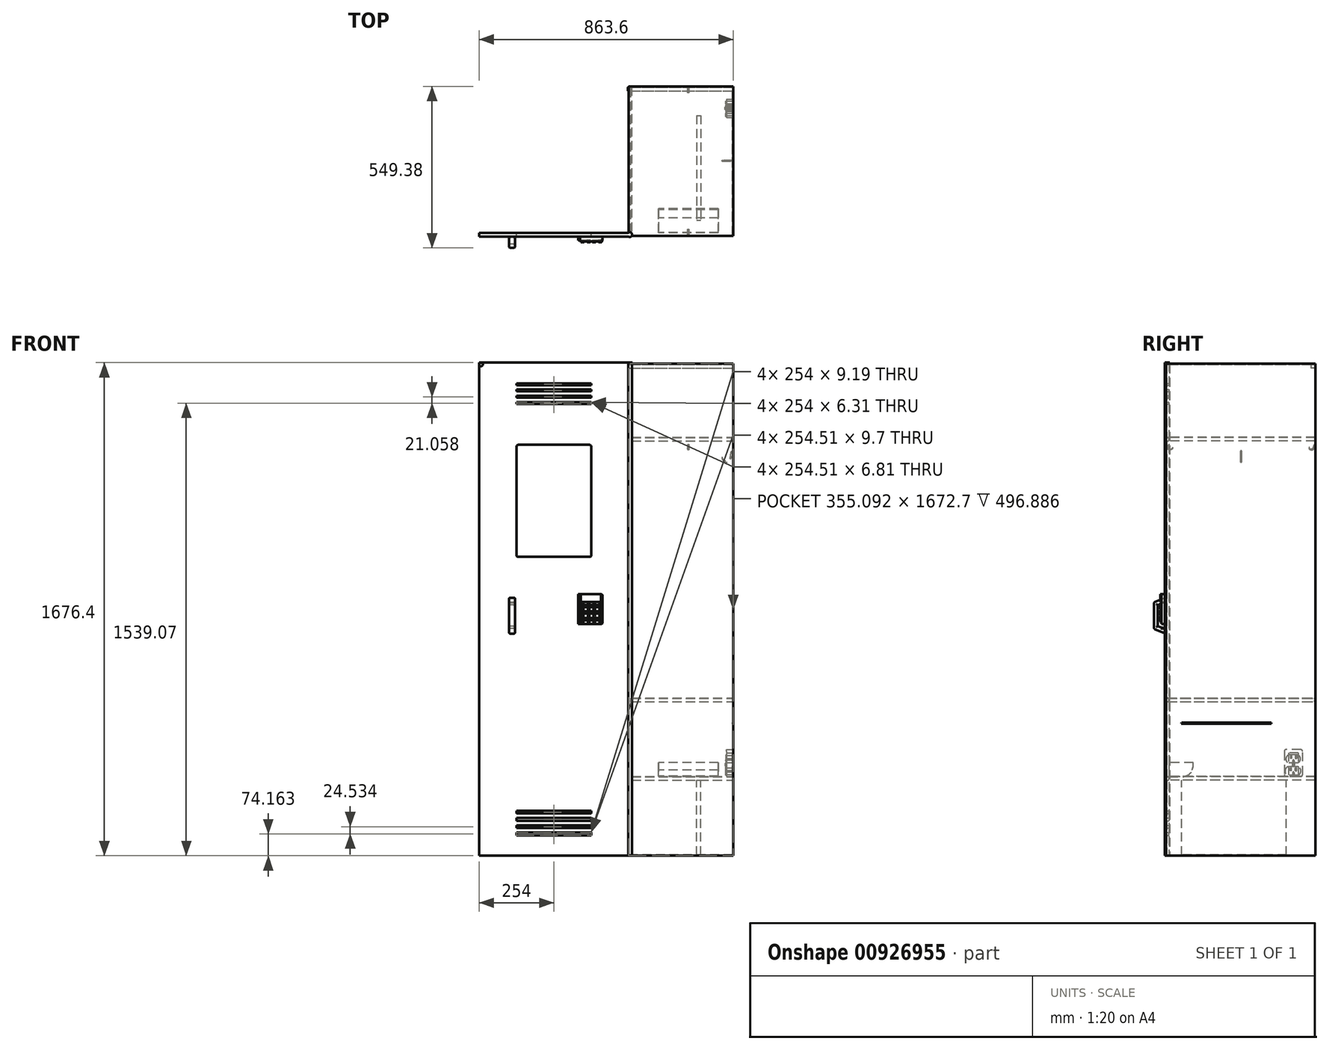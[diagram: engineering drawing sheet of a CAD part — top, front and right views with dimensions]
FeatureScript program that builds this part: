
annotation { "Feature Type Name" : "Feature", "Feature Type Description" : "" }
export const myFeature = defineFeature(function(context is Context, id is Id, definition is map)
    precondition{}
    {
        {
            var Q0;
            Q0=qCreatedBy(makeId("Front.planeOp"),FACE);
            var sketch = newSketch(context, id + "F0", { "sketchPlane" : qUnion([Q0])});
            skLineSegment(sketch, "E0.bottom", {"start": v(0, 0) * mm, "end": v(-508, 0) * mm});
            skLineSegment(sketch, "E0.top", {"start": v(0, 1676.4) * mm, "end": v(-508, 1676.4) * mm});
            skLineSegment(sketch, "E0.left", {"start": v(0, 0) * mm, "end": v(0, 1676.4) * mm});
            skLineSegment(sketch, "E0.right", {"start": v(-508, 0) * mm, "end": v(-508, 1676.4) * mm});
            skLineSegment(sketch, "E1", {"start": v(0, 1676.4) * mm, "end": v(0, 838.2) * mm, "construction": true});
            skLineSegment(sketch, "E2", {"start": v(0, 838.2) * mm, "end": v(0, 1257.3) * mm, "construction": true});
            skLineSegment(sketch, "E3", {"start": v(0, 0) * mm, "end": v(0, 838.2) * mm, "construction": true});
            skLineSegment(sketch, "E4", {"start": v(0, 838.2) * mm, "end": v(0, 419.1) * mm, "construction": true});
            skLineSegment(sketch, "E5", {"start": v(0, 0) * mm, "end": v(-254, 0) * mm, "construction": true});
            skLineSegment(sketch, "E6", {"start": v(-127, 0) * mm, "end": v(-381, 0) * mm, "construction": true});
            skLineSegment(sketch, "E7", {"start": v(-127, 0) * mm, "end": v(-127, 838.2) * mm, "construction": true});
            skLineSegment(sketch, "E8", {"start": v(-381, 0) * mm, "end": v(-381, 838.2) * mm, "construction": true});
            skLineSegment(sketch, "E9", {"start": v(-374.65, 1397) * mm, "end": v(-133.35, 1397) * mm});
            skLineSegment(sketch, "E10", {"start": v(-127, 1390.65) * mm, "end": v(-127, 1021.08) * mm});
            skLineSegment(sketch, "E11", {"start": v(-132.08, 1016) * mm, "end": v(-375.92, 1016) * mm});
            skLineSegment(sketch, "E12", {"start": v(-381, 1021.08) * mm, "end": v(-381, 1390.65) * mm});
            skPoint(sketch, "E13.visualSharp", {"position": v(-127, 1397) * mm});
            skArc(sketch, "E13.filletArc", {"start": v(-127, 1390.65) * mm, "mid": v(-128.86, 1395.14) * mm, "end": v(-133.35, 1397) * mm});
            skLineSegment(sketch, "E14.bottom", {"start": v(-165.1, 889) * mm, "end": v(-93.98, 889) * mm});
            skLineSegment(sketch, "E14.top", {"start": v(-165.1, 787.4) * mm, "end": v(-93.98, 787.4) * mm});
            skLineSegment(sketch, "E14.left", {"start": v(-165.1, 889) * mm, "end": v(-165.1, 787.4) * mm});
            skLineSegment(sketch, "E14.right", {"start": v(-88.9, 883.92) * mm, "end": v(-88.9, 792.48) * mm});
            skPoint(sketch, "E14.middle", {"position": v(-127, 838.2) * mm});
            skPoint(sketch, "E15.visualSharp", {"position": v(-381, 1397) * mm});
            skArc(sketch, "E15.filletArc", {"start": v(-374.65, 1397) * mm, "mid": v(-379.14, 1395.14) * mm, "end": v(-381, 1390.65) * mm});
            skLineSegment(sketch, "E16", {"start": v(-165.1, 889) * mm, "end": v(-167, 889) * mm, "construction": true});
            skPoint(sketch, "E17.visualSharp", {"position": v(-381, 1016) * mm});
            skArc(sketch, "E17.filletArc", {"start": v(-381, 1021.08) * mm, "mid": v(-379.51, 1017.49) * mm, "end": v(-375.92, 1016) * mm});
            skPoint(sketch, "E18.visualSharp", {"position": v(-127, 1016) * mm});
            skArc(sketch, "E18.filletArc", {"start": v(-132.08, 1016) * mm, "mid": v(-128.49, 1017.49) * mm, "end": v(-127, 1021.08) * mm});
            skLineSegment(sketch, "E19", {"start": v(-167, 889) * mm, "end": v(-167, 787.4) * mm});
            skLineSegment(sketch, "E20", {"start": v(-167, 787.4) * mm, "end": v(-172.09, 787.4) * mm});
            skLineSegment(sketch, "E21.bottom", {"start": v(-172.09, 787.4) * mm, "end": v(-167, 787.4) * mm});
            skLineSegment(sketch, "E21.top", {"start": v(-172.09, 889) * mm, "end": v(-167, 889) * mm});
            skLineSegment(sketch, "E21.left", {"start": v(-172.09, 787.4) * mm, "end": v(-172.09, 889) * mm});
            skLineSegment(sketch, "E21.right", {"start": v(-167, 787.4) * mm, "end": v(-167, 889) * mm});
            skLineSegment(sketch, "E22.bottom", {"start": v(-381, 69.57) * mm, "end": v(-127, 69.57) * mm});
            skLineSegment(sketch, "E22.top", {"start": v(-381, 78.76) * mm, "end": v(-127, 78.76) * mm});
            skLineSegment(sketch, "E22.left", {"start": v(-381, 69.57) * mm, "end": v(-381, 78.76) * mm});
            skLineSegment(sketch, "E22.right", {"start": v(-127, 69.57) * mm, "end": v(-127, 78.76) * mm});
            skPoint(sketch, "E23.visualSharp", {"position": v(-88.9, 889) * mm});
            skArc(sketch, "E23.filletArc", {"start": v(-88.9, 883.92) * mm, "mid": v(-90.39, 887.51) * mm, "end": v(-93.98, 889) * mm});
            skPoint(sketch, "E24.visualSharp", {"position": v(-88.9, 787.4) * mm});
            skArc(sketch, "E24.filletArc", {"start": v(-93.98, 787.4) * mm, "mid": v(-90.39, 788.89) * mm, "end": v(-88.9, 792.48) * mm});
            skLineSegment(sketch, "E25", {"start": v(-381, 86.43) * mm, "end": v(-127, 86.43) * mm, "construction": true});
            skLineSegment(sketch, "E26.MirrorCS", {"start": v(-381, 94.1) * mm, "end": v(-127, 94.1) * mm});
            skLineSegment(sketch, "E27.MirrorCS", {"start": v(-381, 103.3) * mm, "end": v(-127, 103.3) * mm});
            skLineSegment(sketch, "E28", {"start": v(-127, 103.3) * mm, "end": v(-127, 94.1) * mm});
            skLineSegment(sketch, "E29", {"start": v(-127, 78.76) * mm, "end": v(-127, 69.57) * mm});
            skLineSegment(sketch, "E30", {"start": v(-381, 103.3) * mm, "end": v(-381, 94.1) * mm});
            skLineSegment(sketch, "E31", {"start": v(-381, 78.76) * mm, "end": v(-381, 69.57) * mm});
            skLineSegment(sketch, "E32", {"start": v(-381, 111.14) * mm, "end": v(-127, 111.14) * mm, "construction": true});
            skLineSegment(sketch, "E33.MirrorCS", {"start": v(-381, 118.98) * mm, "end": v(-127, 118.98) * mm});
            skLineSegment(sketch, "E34.MirrorCS", {"start": v(-381, 128.17) * mm, "end": v(-127, 128.17) * mm});
            skLineSegment(sketch, "E35.MirrorCS", {"start": v(-381, 143.51) * mm, "end": v(-127, 143.51) * mm});
            skLineSegment(sketch, "E36.MirrorCS", {"start": v(-381, 152.7) * mm, "end": v(-127, 152.7) * mm});
            skLineSegment(sketch, "E37", {"start": v(-381, 143.51) * mm, "end": v(-381, 152.7) * mm});
            skLineSegment(sketch, "E38", {"start": v(-127, 152.7) * mm, "end": v(-127, 143.51) * mm});
            skLineSegment(sketch, "E39", {"start": v(-127, 128.17) * mm, "end": v(-127, 118.98) * mm});
            skLineSegment(sketch, "E40", {"start": v(-381, 128.17) * mm, "end": v(-381, 118.98) * mm});
            skLineSegment(sketch, "E41", {"start": v(-381, 1397) * mm, "end": v(-381, 1535.92) * mm, "construction": true});
            skLineSegment(sketch, "E42", {"start": v(-127, 1397) * mm, "end": v(-127, 1557.73) * mm, "construction": true});
            skLineSegment(sketch, "E43.bottom", {"start": v(-381, 1535.92) * mm, "end": v(-127, 1535.92) * mm});
            skLineSegment(sketch, "E43.top", {"start": v(-381, 1542.22) * mm, "end": v(-127, 1542.22) * mm});
            skLineSegment(sketch, "E43.left", {"start": v(-381, 1535.92) * mm, "end": v(-381, 1542.22) * mm});
            skLineSegment(sketch, "E43.right", {"start": v(-127, 1535.92) * mm, "end": v(-127, 1542.22) * mm});
            skLineSegment(sketch, "E44", {"start": v(-127, 1549.6) * mm, "end": v(-381, 1549.6) * mm, "construction": true});
            skLineSegment(sketch, "E45.MirrorCS", {"start": v(-381, 1556.97) * mm, "end": v(-127, 1556.97) * mm});
            skLineSegment(sketch, "E46.MirrorCS", {"start": v(-381, 1563.28) * mm, "end": v(-127, 1563.28) * mm});
            skLineSegment(sketch, "E47", {"start": v(-381, 1563.28) * mm, "end": v(-381, 1556.97) * mm});
            skLineSegment(sketch, "E48", {"start": v(-127, 1563.28) * mm, "end": v(-127, 1557.73) * mm});
            skLineSegment(sketch, "E49", {"start": v(-381.3, 1570.95) * mm, "end": v(-125.33, 1570.95) * mm, "construction": true});
            skLineSegment(sketch, "E50.MirrorCS", {"start": v(-381, 1578.63) * mm, "end": v(-127, 1578.63) * mm});
            skLineSegment(sketch, "E51.MirrorCS", {"start": v(-381, 1584.93) * mm, "end": v(-127, 1584.93) * mm});
            skLineSegment(sketch, "E52.MirrorCS", {"start": v(-381, 1599.69) * mm, "end": v(-127, 1599.69) * mm});
            skLineSegment(sketch, "E53.MirrorCS", {"start": v(-381, 1606) * mm, "end": v(-127, 1606) * mm});
            skLineSegment(sketch, "E54", {"start": v(-381, 1584.93) * mm, "end": v(-381, 1578.63) * mm});
            skLineSegment(sketch, "E55", {"start": v(-381, 1606) * mm, "end": v(-381, 1599.69) * mm});
            skLineSegment(sketch, "E56", {"start": v(-127, 1606) * mm, "end": v(-127, 1599.69) * mm});
            skLineSegment(sketch, "E57", {"start": v(-127, 1584.93) * mm, "end": v(-127, 1578.63) * mm});
            skLineSegment(sketch, "E58", {"start": v(-127, 1556.97) * mm, "end": v(-127, 1563.28) * mm});
            skLineSegment(sketch, "E59", {"start": v(-381, 1556.97) * mm, "end": v(-381, 1563.28) * mm});
            skSolve(sketch);
        }
        {
            var Q0;
            Q0=makeQuery(id+"F0.imprint","IMPRINT",FACE,{"disambiguationData":[TD([[makeQuery(id+"F0.imprint","IMPRINT",EDGE,{"derivedFrom":sQuery(id+"F0.wireOp",EDGE,"E0.bottom")}),-1.0]])]});
            extrude(context, id + "F1", {"entities" : qUnion([Q0]), "depth" : 12.7 * mm, "offsetDistance" : 25.4 * mm});
        }
        {
            var Q0;
            Q0=makeQuery(id+"F0.imprint","IMPRINT",FACE,{"disambiguationData":[TD([[makeQuery(id+"F0.imprint","IMPRINT",EDGE,{"derivedFrom":sQuery(id+"F0.wireOp",EDGE,"E9")}),-1.0]])]});
            extrude(context, id + "F2", {"entities" : qUnion([Q0]), "operationType" : NewBodyOperationType.ADD, "depth" : 12.38 * mm, "offsetDistance" : 25.4 * mm});
        }
        {
            var Q0;
            Q0=makeQuery(id+"F0.imprint","IMPRINT",FACE,{"disambiguationData":[TD([[makeQuery(id+"F0.imprint","IMPRINT",EDGE,{"derivedFrom":sQuery(id+"F0.wireOp",EDGE,"E14.bottom")}),-1.0]])]});
            var Q1;
            Q1=makeQuery(id+"F0.imprint","IMPRINT",FACE,{"disambiguationData":[TD([[makeQuery(id+"F0.imprint","IMPRINT",EDGE,{"derivedFrom":sQuery(id+"F0.wireOp",EDGE,"E19")}),-1.0]])]});
            extrude(context, id + "F3", {"entities" : qUnion([Q0, Q1]), "operationType" : NewBodyOperationType.ADD, "depth" : 25.4 * mm, "offsetDistance" : 25.4 * mm});
        }
        {
            var Q0;
            Q0=makeQuery(id+"F3.opExtrude","CAP_FACE",FACE,{"disambiguationData":[OSD([sQuery(id+"F0.wireOp",EDGE,"E14.bottom"),sQuery(id+"F0.wireOp",EDGE,"E14.top"),sQuery(id+"F0.wireOp",EDGE,"E14.left"),sQuery(id+"F0.wireOp",EDGE,"E14.right"),sQuery(id+"F0.wireOp",EDGE,"E23.filletArc"),sQuery(id+"F0.wireOp",EDGE,"E24.filletArc")])],"isStart":false});
            var sketch = newSketch(context, id + "F4", { "sketchPlane" : qUnion([Q0])});
            skLineSegment(sketch, "E60.bottom", {"start": v(-163, 889) * mm, "end": v(-94.1, 889) * mm});
            skLineSegment(sketch, "E60.top", {"start": v(-163, 862.75) * mm, "end": v(-94.1, 862.75) * mm});
            skLineSegment(sketch, "E60.left", {"start": v(-163, 889) * mm, "end": v(-163, 862.75) * mm});
            skLineSegment(sketch, "E60.right", {"start": v(-94.1, 889) * mm, "end": v(-94.1, 862.75) * mm});
            skLineSegment(sketch, "E61.bottom", {"start": v(-163, 856) * mm, "end": v(-150.3, 856) * mm});
            skLineSegment(sketch, "E61.top", {"start": v(-163, 840.76) * mm, "end": v(-150.3, 840.76) * mm});
            skLineSegment(sketch, "E61.left", {"start": v(-163, 856) * mm, "end": v(-163, 840.76) * mm});
            skLineSegment(sketch, "E61.right", {"start": v(-150.3, 856) * mm, "end": v(-150.3, 840.76) * mm});
            skLineSegment(sketch, "E62", {"start": v(-146.32, 856) * mm, "end": v(-146.32, 837.63) * mm, "construction": true});
            skLineSegment(sketch, "E63", {"start": v(-146.32, 837.63) * mm, "end": v(-160.61, 837.63) * mm, "construction": true});
            skLineSegment(sketch, "E64.MirrorCS", {"start": v(-142.35, 856) * mm, "end": v(-142.35, 840.76) * mm});
            skLineSegment(sketch, "E65.MirrorCS", {"start": v(-129.65, 856) * mm, "end": v(-142.35, 856) * mm});
            skLineSegment(sketch, "E66.MirrorCS", {"start": v(-129.65, 856) * mm, "end": v(-129.65, 840.76) * mm});
            skLineSegment(sketch, "E67.MirrorCS", {"start": v(-129.65, 840.76) * mm, "end": v(-142.35, 840.76) * mm});
            skLineSegment(sketch, "E68.MirrorCS", {"start": v(-163, 834.5) * mm, "end": v(-150.3, 834.5) * mm});
            skLineSegment(sketch, "E69.MirrorCS", {"start": v(-150.3, 819.26) * mm, "end": v(-150.3, 834.5) * mm});
            skLineSegment(sketch, "E70.MirrorCS", {"start": v(-163, 819.26) * mm, "end": v(-150.3, 819.26) * mm});
            skLineSegment(sketch, "E71.MirrorCS", {"start": v(-163, 819.26) * mm, "end": v(-163, 834.5) * mm});
            skLineSegment(sketch, "E72.MirrorCS", {"start": v(-142.35, 819.26) * mm, "end": v(-142.35, 834.5) * mm});
            skLineSegment(sketch, "E73.MirrorCS", {"start": v(-129.65, 819.26) * mm, "end": v(-142.35, 819.26) * mm});
            skLineSegment(sketch, "E74.MirrorCS", {"start": v(-129.65, 819.26) * mm, "end": v(-129.65, 834.5) * mm});
            skLineSegment(sketch, "E75.MirrorCS", {"start": v(-129.65, 834.5) * mm, "end": v(-142.35, 834.5) * mm});
            skLineSegment(sketch, "E76", {"start": v(-126.58, 856) * mm, "end": v(-126.58, 840.76) * mm, "construction": true});
            skLineSegment(sketch, "E77", {"start": v(-161.6, 815.37) * mm, "end": v(-130.5, 815.37) * mm, "construction": true});
            skLineSegment(sketch, "E78.MirrorCS", {"start": v(-123.5, 856) * mm, "end": v(-123.5, 840.76) * mm});
            skLineSegment(sketch, "E79.MirrorCS", {"start": v(-123.5, 840.76) * mm, "end": v(-110.8, 840.76) * mm});
            skLineSegment(sketch, "E80.MirrorCS", {"start": v(-110.8, 856) * mm, "end": v(-110.8, 840.76) * mm});
            skLineSegment(sketch, "E81.MirrorCS", {"start": v(-123.5, 856) * mm, "end": v(-110.8, 856) * mm});
            skLineSegment(sketch, "E82.MirrorCS", {"start": v(-123.5, 819.26) * mm, "end": v(-123.5, 834.5) * mm});
            skLineSegment(sketch, "E83.MirrorCS", {"start": v(-123.5, 819.26) * mm, "end": v(-110.8, 819.26) * mm});
            skLineSegment(sketch, "E84.MirrorCS", {"start": v(-110.8, 819.26) * mm, "end": v(-110.8, 834.5) * mm});
            skLineSegment(sketch, "E85.MirrorCS", {"start": v(-123.5, 834.5) * mm, "end": v(-110.8, 834.5) * mm});
            skLineSegment(sketch, "E86.MirrorCS", {"start": v(-129.65, 811.48) * mm, "end": v(-142.35, 811.48) * mm});
            skLineSegment(sketch, "E87.MirrorCS", {"start": v(-123.5, 811.48) * mm, "end": v(-110.8, 811.48) * mm});
            skLineSegment(sketch, "E88.MirrorCS", {"start": v(-123.5, 811.48) * mm, "end": v(-123.5, 796.24) * mm});
            skLineSegment(sketch, "E89.MirrorCS", {"start": v(-123.5, 796.24) * mm, "end": v(-110.8, 796.24) * mm});
            skLineSegment(sketch, "E90.MirrorCS", {"start": v(-110.8, 811.48) * mm, "end": v(-110.8, 796.24) * mm});
            skLineSegment(sketch, "E91.MirrorCS", {"start": v(-129.65, 811.48) * mm, "end": v(-129.65, 796.24) * mm});
            skLineSegment(sketch, "E92.MirrorCS", {"start": v(-129.65, 796.24) * mm, "end": v(-142.35, 796.24) * mm});
            skLineSegment(sketch, "E93.MirrorCS", {"start": v(-142.35, 811.48) * mm, "end": v(-142.35, 796.24) * mm});
            skLineSegment(sketch, "E94.MirrorCS", {"start": v(-150.3, 811.48) * mm, "end": v(-150.3, 796.24) * mm});
            skLineSegment(sketch, "E95.MirrorCS", {"start": v(-163, 796.24) * mm, "end": v(-150.3, 796.24) * mm});
            skLineSegment(sketch, "E96.MirrorCS", {"start": v(-163, 811.48) * mm, "end": v(-163, 796.24) * mm});
            skLineSegment(sketch, "E97.MirrorCS", {"start": v(-163, 811.48) * mm, "end": v(-150.3, 811.48) * mm});
            skLineSegment(sketch, "E98.MirrorCS", {"start": v(-102.86, 856) * mm, "end": v(-102.86, 840.76) * mm});
            skLineSegment(sketch, "E99.MirrorCS", {"start": v(-90.16, 856) * mm, "end": v(-90.16, 840.76) * mm});
            skLineSegment(sketch, "E100.MirrorCS", {"start": v(-90.16, 856) * mm, "end": v(-102.86, 856) * mm});
            skLineSegment(sketch, "E101.MirrorCS", {"start": v(-90.16, 840.76) * mm, "end": v(-102.86, 840.76) * mm});
            skLineSegment(sketch, "E102.MirrorCS", {"start": v(-102.86, 819.26) * mm, "end": v(-102.86, 834.5) * mm});
            skLineSegment(sketch, "E103.MirrorCS", {"start": v(-90.16, 819.26) * mm, "end": v(-102.86, 819.26) * mm});
            skLineSegment(sketch, "E104.MirrorCS", {"start": v(-90.16, 819.26) * mm, "end": v(-90.16, 834.5) * mm});
            skLineSegment(sketch, "E105.MirrorCS", {"start": v(-90.16, 834.5) * mm, "end": v(-102.86, 834.5) * mm});
            skLineSegment(sketch, "E106.MirrorCS", {"start": v(-102.86, 811.48) * mm, "end": v(-102.86, 796.24) * mm});
            skLineSegment(sketch, "E107.MirrorCS", {"start": v(-90.16, 811.48) * mm, "end": v(-102.86, 811.48) * mm});
            skLineSegment(sketch, "E108.MirrorCS", {"start": v(-90.16, 811.48) * mm, "end": v(-90.16, 796.24) * mm});
            skLineSegment(sketch, "E109.MirrorCS", {"start": v(-90.16, 796.24) * mm, "end": v(-102.86, 796.24) * mm});
            skSolve(sketch);
        }
        {
            var Q0;
            Q0 = qSketchRegion(id + "F4", true);
            extrude(context, id + "F5", {"entities" : qUnion([Q0]), "operationType" : NewBodyOperationType.ADD, "depth" : 3.8 * mm, "offsetDistance" : 25.4 * mm});
        }
        {
            var Q0;
            Q0=qCreatedBy(makeId("Right.planeOp"),FACE);
            cPlane(context, id + "F6", {"entities" : qUnion([Q0]), "cplaneType" : CPlaneType.OFFSET, "offset" : 406.4 * mm, "oppositeDirection" : true, "width" : 152.4 * mm, "height" : 152.4 * mm});
        }
        {
            var Q0;
            Q0=makeQuery(id+"F5.opExtrude","CAP_FACE",FACE,{"disambiguationData":[OSD([sQuery(id+"F4.wireOp",EDGE,"E61.bottom"),sQuery(id+"F4.wireOp",EDGE,"E61.top"),sQuery(id+"F4.wireOp",EDGE,"E61.left"),sQuery(id+"F4.wireOp",EDGE,"E61.right")])],"isStart":false});
            var sketch = newSketch(context, id + "F7", { "sketchPlane" : qUnion([Q0])});
            skText(sketch, "E110", { "text": "0\n", "fontName": "OpenSans-Regular.ttf"});
            skText(sketch, "E111", { "text": "1\n", "fontName": "OpenSans-Regular.ttf"});
            skText(sketch, "E112", { "text": "2\n", "fontName": "OpenSans-Regular.ttf"});
            skText(sketch, "E113", { "text": "3\n", "fontName": "OpenSans-Regular.ttf"});
            skText(sketch, "E114", { "text": "4\n", "fontName": "OpenSans-Regular.ttf"});
            skText(sketch, "E115", { "text": "5\n", "fontName": "OpenSans-Regular.ttf"});
            skText(sketch, "E116", { "text": "6\n", "fontName": "OpenSans-Regular.ttf"});
            skText(sketch, "E117", { "text": "7\n", "fontName": "OpenSans-Regular.ttf"});
            skText(sketch, "E118", { "text": "8\n", "fontName": "OpenSans-Regular.ttf"});
            skText(sketch, "E119", { "text": "9\n", "fontName": "OpenSans-Regular.ttf"});
            skLineSegment(sketch, "E120", {"start": v(-123.45, 804.34) * mm, "end": v(-119.4, 798.9) * mm});
            skLineSegment(sketch, "E121", {"start": v(-119.4, 798.9) * mm, "end": v(-111.54, 810.93) * mm});
            skLineSegment(sketch, "E122", {"start": v(-123.45, 804.34) * mm, "end": v(-120.71, 806.37) * mm});
            skLineSegment(sketch, "E123", {"start": v(-120.71, 806.37) * mm, "end": v(-119.2, 804.34) * mm});
            skLineSegment(sketch, "E124", {"start": v(-119.2, 804.34) * mm, "end": v(-114.6, 812.1) * mm});
            skLineSegment(sketch, "E125", {"start": v(-114.6, 812.1) * mm, "end": v(-111.54, 810.93) * mm});
            skLineSegment(sketch, "E126", {"start": v(-100.09, 809.82) * mm, "end": v(-100.09, 807.36) * mm});
            skLineSegment(sketch, "E127", {"start": v(-100.09, 807.36) * mm, "end": v(-102.24, 807.36) * mm});
            skLineSegment(sketch, "E128", {"start": v(-102.24, 807.36) * mm, "end": v(-102.25, 805.19) * mm});
            skLineSegment(sketch, "E129", {"start": v(-102.25, 805.19) * mm, "end": v(-100.45, 805.18) * mm});
            skLineSegment(sketch, "E130", {"start": v(-100.45, 805.18) * mm, "end": v(-100.45, 802.4) * mm});
            skLineSegment(sketch, "E131", {"start": v(-100.45, 802.4) * mm, "end": v(-102.19, 802.4) * mm});
            skLineSegment(sketch, "E132", {"start": v(-102.19, 802.4) * mm, "end": v(-102.19, 799.35) * mm});
            skLineSegment(sketch, "E133", {"start": v(-102.19, 799.35) * mm, "end": v(-99.7, 799.35) * mm});
            skLineSegment(sketch, "E134", {"start": v(-99.7, 799.35) * mm, "end": v(-99.7, 796.65) * mm});
            skLineSegment(sketch, "E135", {"start": v(-99.7, 796.65) * mm, "end": v(-97.8, 796.65) * mm});
            skLineSegment(sketch, "E136", {"start": v(-97.8, 796.65) * mm, "end": v(-97.8, 798.72) * mm});
            skLineSegment(sketch, "E137", {"start": v(-97.8, 798.72) * mm, "end": v(-95.46, 798.72) * mm});
            skLineSegment(sketch, "E138", {"start": v(-95.46, 798.72) * mm, "end": v(-95.46, 796.56) * mm});
            skLineSegment(sketch, "E139", {"start": v(-95.46, 796.56) * mm, "end": v(-93.33, 796.56) * mm});
            skLineSegment(sketch, "E140", {"start": v(-93.33, 796.56) * mm, "end": v(-93.33, 798.77) * mm});
            skLineSegment(sketch, "E141", {"start": v(-93.33, 798.77) * mm, "end": v(-91.11, 798.77) * mm});
            skLineSegment(sketch, "E142", {"start": v(-91.11, 798.77) * mm, "end": v(-91.11, 802.37) * mm});
            skLineSegment(sketch, "E143", {"start": v(-91.11, 802.37) * mm, "end": v(-93.25, 802.37) * mm});
            skLineSegment(sketch, "E144", {"start": v(-93.25, 802.37) * mm, "end": v(-93.25, 804.6) * mm});
            skLineSegment(sketch, "E145", {"start": v(-93.25, 804.6) * mm, "end": v(-91.4, 804.6) * mm});
            skLineSegment(sketch, "E146", {"start": v(-91.4, 804.6) * mm, "end": v(-91.4, 807.67) * mm});
            skLineSegment(sketch, "E147", {"start": v(-91.4, 807.67) * mm, "end": v(-93.75, 807.67) * mm});
            skLineSegment(sketch, "E148", {"start": v(-93.75, 807.67) * mm, "end": v(-93.75, 809.78) * mm});
            skLineSegment(sketch, "E149", {"start": v(-93.75, 809.78) * mm, "end": v(-95.72, 809.78) * mm});
            skLineSegment(sketch, "E150", {"start": v(-95.72, 809.78) * mm, "end": v(-95.72, 807.67) * mm});
            skLineSegment(sketch, "E151", {"start": v(-95.72, 807.67) * mm, "end": v(-97.34, 807.67) * mm});
            skLineSegment(sketch, "E152", {"start": v(-97.34, 807.67) * mm, "end": v(-97.34, 809.66) * mm});
            skLineSegment(sketch, "E153", {"start": v(-97.34, 809.66) * mm, "end": v(-100.09, 809.82) * mm});
            skLineSegment(sketch, "E154", {"start": v(-98.2, 805.01) * mm, "end": v(-98.2, 802.37) * mm});
            skLineSegment(sketch, "E155", {"start": v(-98.2, 802.37) * mm, "end": v(-95.72, 802.37) * mm});
            skLineSegment(sketch, "E156", {"start": v(-95.72, 802.37) * mm, "end": v(-95.72, 804.9) * mm});
            skLineSegment(sketch, "E157", {"start": v(-95.72, 804.9) * mm, "end": v(-98.2, 805.01) * mm});
            const initialGuessF7  = {"E110": [-0.163, 0.84076, 1, 0, 0.01524], "E111": [-0.14134, 0.84105, 1, 0, 0.01498], "E112": [-0.12275, 0.84156, 1, 0, 0.01481], "E113": [-0.10298, 0.84115, 1, 0, 0.01538], "E114": [-0.1628, 0.81912, 1, 0, 0.01586], "E115": [-0.14211, 0.81917, 1, 0, 0.01584], "E116": [-0.12345, 0.81968, 1, 0, 0.01433], "E117": [-0.1028, 0.81978, 1, 0, 0.01503], "E118": [-0.16265, 0.79707, 1, 0, 0.01493], "E119": [-0.14154, 0.79678, 1, 0, 0.01531]};
            skSetInitialGuess(sketch, initialGuessF7);
            skSolve(sketch);
        }
        {
            var Q0;
            Q0 = qSketchRegion(id + "F7", true);
            extrude(context, id + "F8", {"entities" : qUnion([Q0]), "operationType" : NewBodyOperationType.ADD, "depth" : 2.54 * mm, "offsetDistance" : 25.4 * mm});
        }
        {
            var Q0;
            Q0=qCreatedBy(id+"F6.planeOp",FACE);
            var sketch = newSketch(context, id + "F9", { "sketchPlane" : qUnion([Q0])});
            skLineSegment(sketch, "E158", {"start": v(-13.5, 877.84) * mm, "end": v(-13.5, 860.93) * mm});
            skLineSegment(sketch, "E159", {"start": v(-13.5, 860.93) * mm, "end": v(-13.5, 772.03) * mm, "construction": true});
            skLineSegment(sketch, "E160", {"start": v(-13.5, 772.03) * mm, "end": v(-13.5, 755.11) * mm});
            skLineSegment(sketch, "E161", {"start": v(-13.5, 816.48) * mm, "end": v(-51.6, 816.48) * mm, "construction": true});
            skLineSegment(sketch, "E162", {"start": v(-51.6, 816.48) * mm, "end": v(-51.6, 860.93) * mm});
            skLineSegment(sketch, "E163", {"start": v(-51.6, 860.93) * mm, "end": v(-13.5, 877.84) * mm});
            skLineSegment(sketch, "E164", {"start": v(-13.5, 860.93) * mm, "end": v(-38.4, 852.21) * mm});
            skLineSegment(sketch, "E165", {"start": v(-38.4, 852.21) * mm, "end": v(-38.4, 816.48) * mm});
            skLineSegment(sketch, "E166.MirrorCS", {"start": v(-38.4, 780.75) * mm, "end": v(-38.4, 816.48) * mm});
            skLineSegment(sketch, "E167.MirrorCS", {"start": v(-51.6, 816.48) * mm, "end": v(-51.6, 772.03) * mm});
            skLineSegment(sketch, "E168.MirrorCS", {"start": v(-51.6, 772.03) * mm, "end": v(-13.5, 755.11) * mm});
            skLineSegment(sketch, "E169.MirrorCS", {"start": v(-13.5, 772.03) * mm, "end": v(-38.4, 780.75) * mm});
            skLineSegment(sketch, "E170", {"start": v(-13.5, 772.03) * mm, "end": v(-11.28, 772.03) * mm});
            skLineSegment(sketch, "E171", {"start": v(-11.28, 772.03) * mm, "end": v(-11.28, 755.68) * mm});
            skLineSegment(sketch, "E172", {"start": v(-11.28, 755.68) * mm, "end": v(-13.5, 755.11) * mm});
            skLineSegment(sketch, "E173", {"start": v(-13.5, 877.84) * mm, "end": v(-11.55, 876.67) * mm});
            skLineSegment(sketch, "E174", {"start": v(-11.55, 876.67) * mm, "end": v(-11.55, 860.7) * mm});
            skLineSegment(sketch, "E175", {"start": v(-11.55, 860.7) * mm, "end": v(-13.5, 860.93) * mm});
            skSolve(sketch);
        }
        {
            var Q0;
            Q0 = qSketchRegion(id + "F9", true);
            extrude(context, id + "F10", {"entities" : qUnion([Q0]), "depth" : 20.32 * mm, "offsetDistance" : 25.4 * mm});
        }
        {
            var Q0;
            Q0=qCreatedBy(makeId("Top.planeOp"),FACE);
            var sketch = newSketch(context, id + "F11", { "sketchPlane" : qUnion([Q0])});
            skCircle(sketch, "E176", {"center": v(3.96, -6.27) * mm, "radius": 8.1 * mm});
            skSolve(sketch);
        }
        {
            var Q0;
            Q0 = qSketchRegion(id + "F11", true);
            extrude(context, id + "F12", {"entities" : qUnion([Q0]), "operationType" : NewBodyOperationType.ADD, "depth" : 1676.4 * mm, "offsetDistance" : 25.4 * mm});
        }
        {
            var Q0;
            Q0=qCreatedBy(makeId("Right.planeOp"),FACE);
            var sketch = newSketch(context, id + "F13", { "sketchPlane" : qUnion([Q0])});
            skLineSegment(sketch, "E177.left", {"start": v(0, 0) * mm, "end": v(0, 1461.36) * mm});
            skLineSegment(sketch, "E178.right", {"start": v(0, 1461.36) * mm, "end": v(0, 0) * mm, "construction": true});
            skLineSegment(sketch, "E179.right", {"start": v(-10.2, 1673.2) * mm, "end": v(2.01, 0) * mm});
            skLineSegment(sketch, "E180.bottom", {"start": v(-10.2, 1673.2) * mm, "end": v(497.8, 1673.2) * mm});
            skLineSegment(sketch, "E180.top", {"start": v(-10.2, 0) * mm, "end": v(497.8, 0) * mm});
            skLineSegment(sketch, "E180.left", {"start": v(-10.2, 1673.2) * mm, "end": v(-10.2, 0) * mm});
            skLineSegment(sketch, "E180.right", {"start": v(497.8, 1673.2) * mm, "end": v(497.8, 0) * mm});
            skSolve(sketch);
        }
        {
            var Q0;
            Q0 = qSketchRegion(id + "F13", true);
            extrude(context, id + "F14", {"entities" : qUnion([Q0]), "depth" : 355.6 * mm, "offsetDistance" : 25.4 * mm});
        }
        {
            var Q0;
            Q0=makeQuery(id+"F14.opExtrude","CAP_FACE",FACE,{"disambiguationData":[OSD([sQuery(id+"F13.wireOp",EDGE,"E180.bottom"),sQuery(id+"F13.wireOp",EDGE,"E180.top"),sQuery(id+"F13.wireOp",EDGE,"E180.left"),sQuery(id+"F13.wireOp",EDGE,"E180.right")])],"isStart":true});
            shell(context, id + "F15", {"entities" : qUnion([Q0]), "thickness" : 2.54 * mm});
        }
        {
            var Q0;
            Q0=makeQuery(id+"F15.opShell","OFFSET_FACE",FACE,{"disambiguationData":[OSD([sQuery(id+"F13.wireOp",EDGE,"E180.bottom"),sQuery(id+"F13.wireOp",EDGE,"E180.top"),sQuery(id+"F13.wireOp",EDGE,"E180.left"),sQuery(id+"F13.wireOp",EDGE,"E180.right")])]});
            var sketch = newSketch(context, id + "F16", { "sketchPlane" : qUnion([Q0])});
            skLineSegment(sketch, "E181.bottom", {"start": v(-495.25, 1409.7) * mm, "end": v(7.67, 1409.7) * mm});
            skLineSegment(sketch, "E181.top", {"start": v(-495.25, 1422.4) * mm, "end": v(7.67, 1422.4) * mm});
            skLineSegment(sketch, "E181.left", {"start": v(-495.25, 1409.7) * mm, "end": v(-495.25, 1422.4) * mm});
            skLineSegment(sketch, "E181.right", {"start": v(7.67, 1409.7) * mm, "end": v(7.67, 1422.4) * mm});
            skLineSegment(sketch, "E182.bottom", {"start": v(7.67, 535.94) * mm, "end": v(-495.25, 535.94) * mm});
            skLineSegment(sketch, "E182.top", {"start": v(7.67, 523.24) * mm, "end": v(-495.25, 523.24) * mm});
            skLineSegment(sketch, "E182.left", {"start": v(7.67, 535.94) * mm, "end": v(7.67, 523.24) * mm});
            skLineSegment(sketch, "E182.right", {"start": v(-495.25, 535.94) * mm, "end": v(-495.25, 523.24) * mm});
            skLineSegment(sketch, "E183.top", {"start": v(-495.25, 256.54) * mm, "end": v(7.67, 256.54) * mm});
            skLineSegment(sketch, "E183.left", {"start": v(-495.25, 256.54) * mm, "end": v(-495.25, 248.82) * mm});
            skLineSegment(sketch, "E183.right", {"start": v(7.67, 256.54) * mm, "end": v(7.67, 248.82) * mm});
            skLineSegment(sketch, "E184", {"start": v(-495.25, 256.54) * mm, "end": v(-495.25, 2.54) * mm, "construction": true});
            skLineSegment(sketch, "E185", {"start": v(-495.25, 256.54) * mm, "end": v(-495.25, 269.24) * mm, "construction": true});
            skLineSegment(sketch, "E186", {"start": v(-495.25, 269.24) * mm, "end": v(7.67, 269.24) * mm});
            skLineSegment(sketch, "E187", {"start": v(7.67, 269.24) * mm, "end": v(7.67, 256.54) * mm});
            skLineSegment(sketch, "E188", {"start": v(-495.25, 269.24) * mm, "end": v(-495.25, 256.54) * mm});
            skLineSegment(sketch, "E189", {"start": v(-495.25, 269.24) * mm, "end": v(-495.25, 523.24) * mm, "construction": true});
            skLineSegment(sketch, "E190.bottom", {"start": v(-495.25, 1670.67) * mm, "end": v(-482.55, 1670.67) * mm});
            skLineSegment(sketch, "E190.top", {"start": v(-495.25, 1657.97) * mm, "end": v(-482.55, 1657.97) * mm});
            skLineSegment(sketch, "E190.left", {"start": v(-495.25, 1670.67) * mm, "end": v(-495.25, 1657.97) * mm});
            skLineSegment(sketch, "E190.right", {"start": v(-482.55, 1670.67) * mm, "end": v(-482.55, 1657.97) * mm});
            skSolve(sketch);
        }
        {
            var Q0;
            Q0 = qSketchRegion(id + "F16", true);
            extrude(context, id + "F17", {"entities" : qUnion([Q0]), "operationType" : NewBodyOperationType.ADD, "depth" : 342.9 * mm, "offsetDistance" : 25.4 * mm});
        }
        {
            var Q0;
            {var subQ0=sQuery(id+"F13.wireOp",EDGE,"E180.left");var subQ1=sQuery(id+"F13.wireOp",EDGE,"E180.right");Q0=makeQuery(id+"F17.boolean.opBoolean","SPLIT",FACE,{"disambiguationData":[TD([makeQuery(id+"F17.opExtrude","SWEPT_FACE",FACE,{"disambiguationData":[OSD([sQuery(id+"F16.wireOp",EDGE,"E182.top")])]})])],"derivedFrom":makeQuery(id+"F15.opShell","OFFSET_FACE",FACE,{"disambiguationData":[OSD([sQuery(id+"F13.wireOp",EDGE,"E180.bottom"),sQuery(id+"F13.wireOp",EDGE,"E180.top"),subQ0,subQ1])]})});}
            var sketch = newSketch(context, id + "F18", { "sketchPlane" : qUnion([Q0])});
            skLineSegment(sketch, "E191.bottom", {"start": v(-439.43, 350.52) * mm, "end": v(-406.06, 350.52) * mm});
            skLineSegment(sketch, "E191.top", {"start": v(-439.43, 269.24) * mm, "end": v(-406.06, 269.24) * mm});
            skLineSegment(sketch, "E191.left", {"start": v(-439.43, 350.52) * mm, "end": v(-439.43, 269.24) * mm});
            skLineSegment(sketch, "E191.right", {"start": v(-406.06, 350.52) * mm, "end": v(-406.06, 269.24) * mm});
            skLineSegment(sketch, "E192", {"start": v(-439.43, 350.52) * mm, "end": v(-422.75, 350.52) * mm, "construction": true});
            skLineSegment(sketch, "E193", {"start": v(-406.06, 350.52) * mm, "end": v(-422.75, 350.52) * mm, "construction": true});
            skLineSegment(sketch, "E194", {"start": v(-414.4, 350.52) * mm, "end": v(-431.1, 350.52) * mm, "construction": true});
            skLineSegment(sketch, "E195", {"start": v(-431.1, 350.52) * mm, "end": v(-431.1, 269.24) * mm, "construction": true});
            skLineSegment(sketch, "E196", {"start": v(-422.75, 350.52) * mm, "end": v(-422.75, 269.24) * mm, "construction": true});
            skLineSegment(sketch, "E197", {"start": v(-414.4, 350.52) * mm, "end": v(-414.4, 269.24) * mm, "construction": true});
            skLineSegment(sketch, "E198", {"start": v(-439.43, 309.88) * mm, "end": v(-406.06, 309.88) * mm, "construction": true});
            skLineSegment(sketch, "E199", {"start": v(-439.43, 309.88) * mm, "end": v(-439.43, 350.52) * mm, "construction": true});
            skLineSegment(sketch, "E200", {"start": v(-439.43, 330.2) * mm, "end": v(-439.43, 309.88) * mm, "construction": true});
            skLineSegment(sketch, "E201", {"start": v(-439.43, 309.88) * mm, "end": v(-439.43, 269.24) * mm, "construction": true});
            skLineSegment(sketch, "E202", {"start": v(-439.43, 269.24) * mm, "end": v(-439.43, 289.56) * mm, "construction": true});
            skLineSegment(sketch, "E203", {"start": v(-439.43, 289.56) * mm, "end": v(-406.06, 289.56) * mm, "construction": true});
            skLineSegment(sketch, "E204", {"start": v(-439.43, 330.2) * mm, "end": v(-406.06, 330.2) * mm, "construction": true});
            skLineSegment(sketch, "E205", {"start": v(-439.43, 330.2) * mm, "end": v(-439.43, 350.52) * mm, "construction": true});
            skLineSegment(sketch, "E206", {"start": v(-439.43, 320.04) * mm, "end": v(-406.06, 320.04) * mm, "construction": true});
            skLineSegment(sketch, "E207", {"start": v(-439.43, 309.88) * mm, "end": v(-439.43, 289.56) * mm, "construction": true});
            skLineSegment(sketch, "E208", {"start": v(-439.43, 299.72) * mm, "end": v(-406.06, 299.72) * mm, "construction": true});
            skLineSegment(sketch, "E209", {"start": v(-439.43, 289.56) * mm, "end": v(-439.43, 269.24) * mm, "construction": true});
            skLineSegment(sketch, "E210", {"start": v(-439.43, 279.4) * mm, "end": v(-406.06, 279.4) * mm, "construction": true});
            skPoint(sketch, "E211.middle", {"position": v(-431.1, 340.36) * mm});
            skLineSegment(sketch, "E212.bottom", {"start": v(-382.73, 309.88) * mm, "end": v(-429.4, 309.88) * mm, "construction": true});
            skLineSegment(sketch, "E212.top", {"start": v(-382.73, 309.88) * mm, "end": v(-429.4, 309.88) * mm, "construction": true});
            skLineSegment(sketch, "E212.left", {"start": v(-382.73, 309.88) * mm, "end": v(-382.73, 309.88) * mm});
            skLineSegment(sketch, "E212.right", {"start": v(-429.4, 309.88) * mm, "end": v(-429.4, 309.88) * mm});
            skPoint(sketch, "E212.middle", {"position": v(-406.06, 309.88) * mm});
            skLineSegment(sketch, "E213.bottom", {"start": v(-428.95, 340.36) * mm, "end": v(-433.23, 340.36) * mm});
            skLineSegment(sketch, "E213.top", {"start": v(-428.95, 330.6) * mm, "end": v(-433.23, 330.6) * mm});
            skLineSegment(sketch, "E213.left", {"start": v(-428.95, 340.36) * mm, "end": v(-428.95, 330.6) * mm});
            skLineSegment(sketch, "E213.right", {"start": v(-433.23, 340.36) * mm, "end": v(-433.23, 330.6) * mm});
            skPoint(sketch, "E213.middle", {"position": v(-431.1, 335.48) * mm});
            skLineSegment(sketch, "E214.bottom", {"start": v(-425.16, 322.88) * mm, "end": v(-420.33, 322.88) * mm});
            skLineSegment(sketch, "E214.top", {"start": v(-425.16, 317.2) * mm, "end": v(-420.33, 317.2) * mm});
            skLineSegment(sketch, "E214.left", {"start": v(-425.16, 322.88) * mm, "end": v(-425.16, 317.2) * mm});
            skLineSegment(sketch, "E214.right", {"start": v(-420.33, 322.88) * mm, "end": v(-420.33, 317.2) * mm});
            skPoint(sketch, "E214.middle", {"position": v(-422.75, 320.04) * mm});
            skArc(sketch, "E215", {"start": v(-420.33, 322.88) * mm, "mid": v(-422.75, 325.3) * mm, "end": v(-425.16, 322.88) * mm});
            skLineSegment(sketch, "E216.MirrorCS", {"start": v(-416.55, 340.36) * mm, "end": v(-416.55, 330.6) * mm});
            skLineSegment(sketch, "E217.MirrorCS", {"start": v(-416.55, 330.6) * mm, "end": v(-412.26, 330.6) * mm});
            skLineSegment(sketch, "E218.MirrorCS", {"start": v(-412.26, 340.36) * mm, "end": v(-412.26, 330.6) * mm});
            skLineSegment(sketch, "E219", {"start": v(-416.55, 340.36) * mm, "end": v(-412.26, 340.36) * mm});
            skLineSegment(sketch, "E220", {"start": v(-406.06, 309.88) * mm, "end": v(-406.06, 320.04) * mm, "construction": true});
            skLineSegment(sketch, "E221", {"start": v(-406.06, 314.96) * mm, "end": v(-409.15, 314.96) * mm, "construction": true});
            skLineSegment(sketch, "E222.MirrorCS", {"start": v(-416.55, 289.56) * mm, "end": v(-416.55, 299.31) * mm});
            skLineSegment(sketch, "E223.MirrorCS", {"start": v(-412.26, 289.56) * mm, "end": v(-412.26, 299.31) * mm});
            skLineSegment(sketch, "E224.MirrorCS", {"start": v(-416.55, 289.56) * mm, "end": v(-412.26, 289.56) * mm});
            skLineSegment(sketch, "E225.MirrorCS", {"start": v(-416.55, 299.31) * mm, "end": v(-412.26, 299.31) * mm});
            skLineSegment(sketch, "E226.MirrorCS", {"start": v(-428.95, 289.56) * mm, "end": v(-428.95, 299.31) * mm});
            skLineSegment(sketch, "E227.MirrorCS", {"start": v(-433.23, 289.56) * mm, "end": v(-433.23, 299.31) * mm});
            skLineSegment(sketch, "E228.MirrorCS", {"start": v(-428.95, 299.31) * mm, "end": v(-433.23, 299.31) * mm});
            skLineSegment(sketch, "E229.MirrorCS", {"start": v(-428.95, 289.56) * mm, "end": v(-433.23, 289.56) * mm});
            skLineSegment(sketch, "E230.bottom", {"start": v(-425.16, 282.23) * mm, "end": v(-420.33, 282.23) * mm});
            skLineSegment(sketch, "E230.top", {"start": v(-425.16, 276.57) * mm, "end": v(-420.33, 276.57) * mm});
            skLineSegment(sketch, "E230.left", {"start": v(-425.16, 282.23) * mm, "end": v(-425.16, 276.57) * mm});
            skLineSegment(sketch, "E230.right", {"start": v(-420.33, 282.23) * mm, "end": v(-420.33, 276.57) * mm});
            skPoint(sketch, "E230.middle", {"position": v(-422.75, 279.4) * mm});
            skArc(sketch, "E231", {"start": v(-420.33, 282.23) * mm, "mid": v(-422.75, 284.65) * mm, "end": v(-425.16, 282.23) * mm});
            skSolve(sketch);
        }
        {
            var Q0;
            Q0 = qSketchRegion(id + "F18", true);
            extrude(context, id + "F19", {"entities" : qUnion([Q0]), "operationType" : NewBodyOperationType.ADD, "depth" : 20.32 * mm, "offsetDistance" : 25.4 * mm});
        }
        {
            var Q0;
            Q0=qCreatedBy(makeId("Right.planeOp"),FACE);
            var sketch = newSketch(context, id + "F20", { "sketchPlane" : qUnion([Q0])});
            skArc(sketch, "E232", {"start": v(50.8, 270.81) * mm, "mid": v(67.9, 276.44) * mm, "end": v(78.3, 291.12) * mm});
            skArc(sketch, "E233", {"start": v(78.3, 291.12) * mm, "mid": v(81.83, 303.55) * mm, "end": v(81.86, 316.48) * mm});
            skLineSegment(sketch, "E234", {"start": v(81.86, 316.48) * mm, "end": v(0, 316.48) * mm});
            skLineSegment(sketch, "E235", {"start": v(0, 316.48) * mm, "end": v(0, 270.81) * mm});
            skLineSegment(sketch, "E236", {"start": v(50.8, 268.94) * mm, "end": v(13.18, 268.94) * mm});
            skLineSegment(sketch, "E237", {"start": v(50.8, 270.81) * mm, "end": v(50.8, 268.94) * mm});
            skLineSegment(sketch, "E238", {"start": v(13.18, 268.94) * mm, "end": v(0, 268.94) * mm});
            skLineSegment(sketch, "E239", {"start": v(0, 268.94) * mm, "end": v(0, 270.81) * mm});
            skSolve(sketch);
        }
        {
            var Q0;
            Q0 = qSketchRegion(id + "F20", true);
            extrude(context, id + "F21", {"entities" : qUnion([Q0]), "operationType" : NewBodyOperationType.ADD, "depth" : 304.8 * mm, "offsetDistance" : 25.4 * mm, "hasSecondDirection" : true, "secondDirectionOppositeDirection" : false, "secondDirectionDepth" : 101.6 * mm});
        }
        {
            var Q0;
            Q0=makeQuery(id+"F21.opExtrude","SWEPT_FACE",FACE,{"disambiguationData":[OSD([sQuery(id+"F20.wireOp",EDGE,"E234")])]});
            shell(context, id + "F22", {"entities" : qUnion([Q0]), "thickness" : 0.25 * mm});
        }
        {
            var Q0;
            {var subQ0=sQuery(id+"F13.wireOp",EDGE,"E180.left");var subQ1=sQuery(id+"F13.wireOp",EDGE,"E180.right");Q0=makeQuery(id+"F17.boolean.opBoolean","SPLIT",FACE,{"disambiguationData":[TD([makeQuery(id+"F17.opExtrude","SWEPT_FACE",FACE,{"disambiguationData":[OSD([sQuery(id+"F16.wireOp",EDGE,"E181.bottom")])]})])],"derivedFrom":makeQuery(id+"F15.opShell","OFFSET_FACE",FACE,{"disambiguationData":[OSD([sQuery(id+"F13.wireOp",EDGE,"E180.bottom"),sQuery(id+"F13.wireOp",EDGE,"E180.top"),subQ0,subQ1])]})});}
            var sketch = newSketch(context, id + "F23", { "sketchPlane" : qUnion([Q0])});
            skLineSegment(sketch, "E240", {"start": v(-495.25, 1409.7) * mm, "end": v(7.67, 1409.7) * mm, "construction": true});
            skLineSegment(sketch, "E241", {"start": v(-243.8, 1409.7) * mm, "end": v(-243.8, 1368.18) * mm, "construction": true});
            skFitSpline(sketch, "E242", {"points": [v(-495.25, 1398.9) * mm, v(-491.9, 1394.66) * mm, v(-490.02, 1389.72) * mm, v(-486.02, 1382.66) * mm, v(-478.02, 1383.6) * mm, v(-476.84, 1388.54) * mm], "startDerivative": vector(20.25, -22.57) * mm, "endDerivative": vector(-1.32, 30.8) * mm});
            skFitSpline(sketch, "E243", {"points": [v(-476.84, 1388.54) * mm, v(-475.78, 1387.5) * mm, v(-475.85, 1385.74) * mm, v(-476.76, 1382.87) * mm, v(-478.85, 1381.4) * mm, v(-483.33, 1380) * mm, v(-488.5, 1380.63) * mm, v(-491.73, 1384.7) * mm, v(-495.25, 1388.54) * mm], "startDerivative": vector(16.21, -11.48) * mm, "endDerivative": vector(-24.42, 23.33) * mm});
            skLineSegment(sketch, "E244", {"start": v(-495.25, 1398.9) * mm, "end": v(-495.25, 1388.54) * mm});
            skFitSpline(sketch, "E245.MirrorCS", {"points": [v(7.67, 1398.9) * mm, v(4.32, 1394.66) * mm, v(2.43, 1389.72) * mm, v(-1.57, 1382.66) * mm, v(-9.57, 1383.6) * mm, v(-10.74, 1388.54) * mm], "startDerivative": vector(-20.25, -22.57) * mm, "endDerivative": vector(1.32, 30.8) * mm});
            skFitSpline(sketch, "E246.MirrorCS", {"points": [v(-10.74, 1388.54) * mm, v(-11.8, 1387.5) * mm, v(-11.74, 1385.74) * mm, v(-10.82, 1382.87) * mm, v(-8.73, 1381.4) * mm, v(-4.25, 1380) * mm, v(0.92, 1380.63) * mm, v(4.14, 1384.7) * mm, v(7.67, 1388.54) * mm], "startDerivative": vector(-16.21, -11.48) * mm, "endDerivative": vector(24.42, 23.33) * mm});
            skLineSegment(sketch, "E247.MirrorCS", {"start": v(7.67, 1398.9) * mm, "end": v(7.67, 1388.54) * mm});
            skSolve(sketch);
        }
        {
            var Q0;
            Q0=makeQuery(id+"F19.opExtrude","CAP_FACE",FACE,{"disambiguationData":[OSD([sQuery(id+"F18.wireOp",EDGE,"E191.bottom"),sQuery(id+"F18.wireOp",EDGE,"E191.top"),sQuery(id+"F18.wireOp",EDGE,"E191.left"),sQuery(id+"F18.wireOp",EDGE,"E191.right"),sQuery(id+"F18.wireOp",EDGE,"E213.bottom"),sQuery(id+"F18.wireOp",EDGE,"E213.top"),sQuery(id+"F18.wireOp",EDGE,"E213.left"),sQuery(id+"F18.wireOp",EDGE,"E213.right"),sQuery(id+"F18.wireOp",EDGE,"E214.top"),sQuery(id+"F18.wireOp",EDGE,"E214.left"),sQuery(id+"F18.wireOp",EDGE,"E214.right"),sQuery(id+"F18.wireOp",EDGE,"E215"),sQuery(id+"F18.wireOp",EDGE,"E216.MirrorCS"),sQuery(id+"F18.wireOp",EDGE,"E217.MirrorCS"),sQuery(id+"F18.wireOp",EDGE,"E218.MirrorCS"),sQuery(id+"F18.wireOp",EDGE,"E219"),sQuery(id+"F18.wireOp",EDGE,"E222.MirrorCS"),sQuery(id+"F18.wireOp",EDGE,"E223.MirrorCS"),sQuery(id+"F18.wireOp",EDGE,"E224.MirrorCS"),sQuery(id+"F18.wireOp",EDGE,"E225.MirrorCS"),sQuery(id+"F18.wireOp",EDGE,"E226.MirrorCS"),sQuery(id+"F18.wireOp",EDGE,"E227.MirrorCS"),sQuery(id+"F18.wireOp",EDGE,"E228.MirrorCS"),sQuery(id+"F18.wireOp",EDGE,"E229.MirrorCS"),sQuery(id+"F18.wireOp",EDGE,"E230.top"),sQuery(id+"F18.wireOp",EDGE,"E230.left"),sQuery(id+"F18.wireOp",EDGE,"E230.right"),sQuery(id+"F18.wireOp",EDGE,"E231")])],"isStart":false});
            var sketch = newSketch(context, id + "F24", { "sketchPlane" : qUnion([Q0])});
            skCircle(sketch, "E248", {"center": v(-423.09, 309.88) * mm, "radius": 4.58 * mm});
            skPoint(sketch, "E248.centerSnap0", {"position": v(-439.43, 309.88) * mm});
            skLineSegment(sketch, "E249.bottom", {"start": v(-424, 313.22) * mm, "end": v(-422.17, 313.22) * mm});
            skLineSegment(sketch, "E249.top", {"start": v(-424, 306.54) * mm, "end": v(-422.17, 306.54) * mm});
            skLineSegment(sketch, "E249.left", {"start": v(-424, 313.22) * mm, "end": v(-424, 306.54) * mm});
            skLineSegment(sketch, "E249.right", {"start": v(-422.17, 313.22) * mm, "end": v(-422.17, 306.54) * mm});
            skSolve(sketch);
        }
        {
            var Q0;
            Q0 = qSketchRegion(id + "F24", true);
            extrude(context, id + "F25", {"entities" : qUnion([Q0]), "operationType" : NewBodyOperationType.ADD, "depth" : 5.08 * mm, "offsetDistance" : 25.4 * mm});
        }
        {
            var Q0;
            Q0 = qSketchRegion(id + "F23", true);
            extrude(context, id + "F26", {"entities" : qUnion([Q0]), "operationType" : NewBodyOperationType.ADD, "depth" : 152.4 * mm, "offsetDistance" : 25.4 * mm, "hasSecondDirection" : true, "secondDirectionOppositeDirection" : false, "secondDirectionDepth" : 149.22 * mm});
        }
        {
            var Q0;
            {var subQ0=makeQuery(id+"F17.opExtrude","SWEPT_FACE",FACE,{"disambiguationData":[OSD([sQuery(id+"F16.wireOp",EDGE,"E182.top")])]});var subQ1=sQuery(id+"F13.wireOp",EDGE,"E180.right");var subQ4=sQuery(id+"F13.wireOp",EDGE,"E180.left");var subQ5=makeQuery(id+"F15.opShell","OFFSET_FACE",FACE,{"disambiguationData":[OSD([subQ4])]});Q0=makeQuery(id+"F19.boolean.opBoolean","SPLIT",FACE,{"disambiguationData":[TD([subQ5])],"derivedFrom":makeQuery(id+"F17.boolean.opBoolean","SPLIT",FACE,{"disambiguationData":[TD([subQ0])],"derivedFrom":makeQuery(id+"F15.opShell","OFFSET_FACE",FACE,{"disambiguationData":[OSD([sQuery(id+"F13.wireOp",EDGE,"E180.bottom"),sQuery(id+"F13.wireOp",EDGE,"E180.top"),subQ4,subQ1])]})})});}
            var sketch = newSketch(context, id + "F27", { "sketchPlane" : qUnion([Q0])});
            skLineSegment(sketch, "E250", {"start": v(-439.43, 269.24) * mm, "end": v(-447.3, 269.24) * mm});
            skLineSegment(sketch, "E251", {"start": v(-453.65, 275.6) * mm, "end": v(-453.65, 354.78) * mm});
            skLineSegment(sketch, "E252", {"start": v(-447.3, 361.13) * mm, "end": v(-398.19, 361.13) * mm});
            skLineSegment(sketch, "E253", {"start": v(-391.84, 354.78) * mm, "end": v(-391.84, 275.6) * mm});
            skLineSegment(sketch, "E254", {"start": v(-398.19, 269.24) * mm, "end": v(-406.06, 269.24) * mm});
            skPoint(sketch, "E255.visualSharp", {"position": v(-391.84, 361.13) * mm});
            skArc(sketch, "E255.filletArc", {"start": v(-391.84, 354.78) * mm, "mid": v(-393.7, 359.27) * mm, "end": v(-398.19, 361.13) * mm});
            skPoint(sketch, "E256.visualSharp", {"position": v(-453.65, 361.13) * mm});
            skArc(sketch, "E256.filletArc", {"start": v(-447.3, 361.13) * mm, "mid": v(-451.8, 359.27) * mm, "end": v(-453.65, 354.78) * mm});
            skPoint(sketch, "E257.visualSharp", {"position": v(-453.65, 269.24) * mm});
            skArc(sketch, "E257.filletArc", {"start": v(-453.65, 275.6) * mm, "mid": v(-451.8, 271.1) * mm, "end": v(-447.3, 269.24) * mm});
            skPoint(sketch, "E258.visualSharp", {"position": v(-391.84, 269.24) * mm});
            skArc(sketch, "E258.filletArc", {"start": v(-398.19, 269.24) * mm, "mid": v(-393.7, 271.1) * mm, "end": v(-391.84, 275.6) * mm});
            skSolve(sketch);
        }
        {
            var Q0;
            Q0=makeQuery(id+"F27.imprint","IMPRINT",FACE,{"disambiguationData":[TD([[makeQuery(id+"F27.imprint","IMPRINT",EDGE,{"derivedFrom":sQuery(id+"F27.wireOp",EDGE,"E250")}),1.0]])]});
            extrude(context, id + "F28", {"entities" : qUnion([Q0]), "operationType" : NewBodyOperationType.ADD, "depth" : 20.32 * mm, "offsetDistance" : 25.4 * mm});
        }
        {
            var Q0;
            {var subQ0=makeQuery(id+"F17.opExtrude","SWEPT_FACE",FACE,{"disambiguationData":[OSD([sQuery(id+"F16.wireOp",EDGE,"E182.top")])]});var subQ1=sQuery(id+"F13.wireOp",EDGE,"E180.right");var subQ4=sQuery(id+"F13.wireOp",EDGE,"E180.left");var subQ5=makeQuery(id+"F15.opShell","OFFSET_FACE",FACE,{"disambiguationData":[OSD([subQ4])]});Q0=makeQuery(id+"F19.boolean.opBoolean","SPLIT",FACE,{"disambiguationData":[TD([subQ5])],"derivedFrom":makeQuery(id+"F17.boolean.opBoolean","SPLIT",FACE,{"disambiguationData":[TD([subQ0])],"derivedFrom":makeQuery(id+"F15.opShell","OFFSET_FACE",FACE,{"disambiguationData":[OSD([sQuery(id+"F13.wireOp",EDGE,"E180.bottom"),sQuery(id+"F13.wireOp",EDGE,"E180.top"),subQ4,subQ1])]})})});}
            var sketch = newSketch(context, id + "F29", { "sketchPlane" : qUnion([Q0])});
            skLineSegment(sketch, "E259", {"start": v(-347.13, 452.13) * mm, "end": v(-42.33, 452.13) * mm});
            skLineSegment(sketch, "E260", {"start": v(-347.13, 452.13) * mm, "end": v(-347.13, 448.17) * mm});
            skLineSegment(sketch, "E261", {"start": v(-347.13, 448.17) * mm, "end": v(-41.2, 448.17) * mm});
            skLineSegment(sketch, "E262", {"start": v(-41.2, 448.17) * mm, "end": v(-42.33, 452.13) * mm});
            skSolve(sketch);
        }
        {
            var Q0;
            Q0 = qSketchRegion(id + "F29", true);
            extrude(context, id + "F30", {"entities" : qUnion([Q0]), "operationType" : NewBodyOperationType.REMOVE, "oppositeDirection" : true, "depth" : 25.4 * mm, "offsetDistance" : 25.4 * mm});
        }
        {
            var Q0;
            Q0=makeQuery(id+"F15.opShell","OFFSET_FACE",FACE,{"disambiguationData":[OSD([sQuery(id+"F13.wireOp",EDGE,"E180.left")])]});
            var sketch = newSketch(context, id + "F31", { "sketchPlane" : qUnion([Q0])});
            skLineSegment(sketch, "E263", {"start": v(-355.33, 1377.48) * mm, "end": v(-355.33, 1358.89) * mm});
            skFitSpline(sketch, "E264", {"points": [v(-355.33, 1377.48) * mm, v(-347.66, 1371.62) * mm, v(-345.1, 1360.16) * mm, v(-342.96, 1349.9) * mm, v(-337.68, 1343.6) * mm, v(-327.67, 1342.13) * mm, v(-320.96, 1348.13) * mm, v(-318.27, 1356.08) * mm], "startDerivative": vector(62.75, -32.89) * mm, "endDerivative": vector(14.48, 60.76) * mm});
            skFitSpline(sketch, "E265", {"points": [v(-318.27, 1356.08) * mm, v(-317.29, 1354.1) * mm, v(-317.35, 1351.42) * mm, v(-318.27, 1347.95) * mm, v(-319.86, 1344.97) * mm, v(-322.91, 1341.67) * mm, v(-326.07, 1339.06) * mm, v(-329.96, 1338.23) * mm, v(-336.45, 1337.67) * mm, v(-340.79, 1340.9) * mm, v(-345.15, 1345.6) * mm, v(-350.32, 1356.08) * mm, v(-355.33, 1358.89) * mm], "startDerivative": vector(21.34, -33.3) * mm, "endDerivative": vector(-58.67, 17.36) * mm});
            skSolve(sketch);
        }
        {
            var Q0;
            Q0 = qSketchRegion(id + "F31", true);
            extrude(context, id + "F32", {"entities" : qUnion([Q0]), "operationType" : NewBodyOperationType.ADD, "depth" : 254 * mm, "offsetDistance" : 25.4 * mm, "hasSecondDirection" : true, "secondDirectionOppositeDirection" : false, "secondDirectionDepth" : 250.82 * mm});
        }
        {
            var Q0;
            Q0=makeQuery(id+"F1.opExtrude","SWEPT_BODY",BODY,{"disambiguationData":[OSD([sQuery(id+"F0.wireOp",EDGE,"E0.bottom"),sQuery(id+"F0.wireOp",EDGE,"E0.top"),sQuery(id+"F0.wireOp",EDGE,"E0.left"),sQuery(id+"F0.wireOp",EDGE,"E0.right"),sQuery(id+"F0.wireOp",EDGE,"E9"),sQuery(id+"F0.wireOp",EDGE,"E10"),sQuery(id+"F0.wireOp",EDGE,"E11"),sQuery(id+"F0.wireOp",EDGE,"E12"),sQuery(id+"F0.wireOp",EDGE,"E13.filletArc"),sQuery(id+"F0.wireOp",EDGE,"E14.bottom"),sQuery(id+"F0.wireOp",EDGE,"E14.top"),sQuery(id+"F0.wireOp",EDGE,"E14.left"),sQuery(id+"F0.wireOp",EDGE,"E14.right"),sQuery(id+"F0.wireOp",EDGE,"E15.filletArc"),sQuery(id+"F0.wireOp",EDGE,"E17.filletArc"),sQuery(id+"F0.wireOp",EDGE,"E18.filletArc"),sQuery(id+"F0.wireOp",EDGE,"E19"),sQuery(id+"F0.wireOp",EDGE,"E20"),sQuery(id+"F0.wireOp",EDGE,"E21.top"),sQuery(id+"F0.wireOp",EDGE,"E21.left"),sQuery(id+"F0.wireOp",EDGE,"E22.bottom"),sQuery(id+"F0.wireOp",EDGE,"E22.top"),sQuery(id+"F0.wireOp",EDGE,"E22.left"),sQuery(id+"F0.wireOp",EDGE,"E22.right"),sQuery(id+"F0.wireOp",EDGE,"E23.filletArc"),sQuery(id+"F0.wireOp",EDGE,"E24.filletArc"),sQuery(id+"F0.wireOp",EDGE,"E26.MirrorCS"),sQuery(id+"F0.wireOp",EDGE,"E27.MirrorCS"),sQuery(id+"F0.wireOp",EDGE,"E28"),sQuery(id+"F0.wireOp",EDGE,"E30"),sQuery(id+"F0.wireOp",EDGE,"E33.MirrorCS"),sQuery(id+"F0.wireOp",EDGE,"E34.MirrorCS"),sQuery(id+"F0.wireOp",EDGE,"E35.MirrorCS"),sQuery(id+"F0.wireOp",EDGE,"E36.MirrorCS"),sQuery(id+"F0.wireOp",EDGE,"E37"),sQuery(id+"F0.wireOp",EDGE,"E38"),sQuery(id+"F0.wireOp",EDGE,"E39"),sQuery(id+"F0.wireOp",EDGE,"E40"),sQuery(id+"F0.wireOp",EDGE,"E43.bottom"),sQuery(id+"F0.wireOp",EDGE,"E43.top"),sQuery(id+"F0.wireOp",EDGE,"E43.left"),sQuery(id+"F0.wireOp",EDGE,"E43.right"),sQuery(id+"F0.wireOp",EDGE,"E45.MirrorCS"),sQuery(id+"F0.wireOp",EDGE,"E46.MirrorCS"),sQuery(id+"F0.wireOp",EDGE,"E47"),sQuery(id+"F0.wireOp",EDGE,"E48"),sQuery(id+"F0.wireOp",EDGE,"E50.MirrorCS"),sQuery(id+"F0.wireOp",EDGE,"E51.MirrorCS"),sQuery(id+"F0.wireOp",EDGE,"E52.MirrorCS"),sQuery(id+"F0.wireOp",EDGE,"E53.MirrorCS"),sQuery(id+"F0.wireOp",EDGE,"E54"),sQuery(id+"F0.wireOp",EDGE,"E55"),sQuery(id+"F0.wireOp",EDGE,"E56"),sQuery(id+"F0.wireOp",EDGE,"E57"),sQuery(id+"F0.wireOp",EDGE,"E58")])]});
            var Q1;
            Q1=makeQuery(id+"F10.opExtrude","SWEPT_BODY",BODY,{"disambiguationData":[OSD([sQuery(id+"F9.wireOp",EDGE,"E158"),sQuery(id+"F9.wireOp",EDGE,"E160"),sQuery(id+"F9.wireOp",EDGE,"E162"),sQuery(id+"F9.wireOp",EDGE,"E163"),sQuery(id+"F9.wireOp",EDGE,"E164"),sQuery(id+"F9.wireOp",EDGE,"E165"),sQuery(id+"F9.wireOp",EDGE,"E166.MirrorCS"),sQuery(id+"F9.wireOp",EDGE,"E167.MirrorCS"),sQuery(id+"F9.wireOp",EDGE,"E168.MirrorCS"),sQuery(id+"F9.wireOp",EDGE,"E169.MirrorCS")])]});
            var Q2;
            Q2=makeQuery(id+"F14.opExtrude","SWEPT_BODY",BODY,{"disambiguationData":[OSD([sQuery(id+"F13.wireOp",EDGE,"E180.bottom"),sQuery(id+"F13.wireOp",EDGE,"E180.top"),sQuery(id+"F13.wireOp",EDGE,"E180.left"),sQuery(id+"F13.wireOp",EDGE,"E180.right")])]});
            var Q3;
            Q3=makeQuery(id+"FTfwmO2ZgdWLviC_3.opExtrude","SWEPT_BODY",BODY,{"disambiguationData":[OSD([sQuery(id+"F8G7i9CjAsLjY6p_3.wireOp",EDGE,"dkMLvgdq-jajX-Sxnn-G86Q-O4qEg4DQSTtu.bottom"),sQuery(id+"F8G7i9CjAsLjY6p_3.wireOp",EDGE,"dkMLvgdq-jajX-Sxnn-G86Q-O4qEg4DQSTtu.top"),sQuery(id+"F8G7i9CjAsLjY6p_3.wireOp",EDGE,"dkMLvgdq-jajX-Sxnn-G86Q-O4qEg4DQSTtu.left"),sQuery(id+"F8G7i9CjAsLjY6p_3.wireOp",EDGE,"dkMLvgdq-jajX-Sxnn-G86Q-O4qEg4DQSTtu.right")])]});
            booleanBodies(context, id + "F33", {"operationType" : BooleanOperationType.UNION, "tools" : qUnion([Q0, Q1, Q2, Q3])});
        }
        {
            var Q0;
            {var subQ0=sQuery(id+"F18.wireOp",EDGE,"E191.right");var subQ1=sQuery(id+"F18.wireOp",EDGE,"E191.left");var subQ2=sQuery(id+"F18.wireOp",EDGE,"E191.bottom");var subQ3=sQuery(id+"F18.wireOp",EDGE,"E226.MirrorCS");var subQ4=sQuery(id+"F18.wireOp",EDGE,"E225.MirrorCS");var subQ5=sQuery(id+"F18.wireOp",EDGE,"E224.MirrorCS");var subQ6=sQuery(id+"F18.wireOp",EDGE,"E223.MirrorCS");var subQ7=sQuery(id+"F18.wireOp",EDGE,"E222.MirrorCS");var subQ8=sQuery(id+"F18.wireOp",EDGE,"E219");var subQ9=sQuery(id+"F18.wireOp",EDGE,"E218.MirrorCS");var subQ10=sQuery(id+"F18.wireOp",EDGE,"E217.MirrorCS");var subQ11=sQuery(id+"F18.wireOp",EDGE,"E216.MirrorCS");var subQ12=sQuery(id+"F18.wireOp",EDGE,"E215");var subQ13=sQuery(id+"F18.wireOp",EDGE,"E214.right");var subQ14=sQuery(id+"F18.wireOp",EDGE,"E227.MirrorCS");var subQ15=sQuery(id+"F18.wireOp",EDGE,"E214.left");var subQ16=sQuery(id+"F18.wireOp",EDGE,"E213.right");var subQ17=sQuery(id+"F18.wireOp",EDGE,"E214.top");var subQ18=sQuery(id+"F18.wireOp",EDGE,"E213.bottom");var subQ19=sQuery(id+"F18.wireOp",EDGE,"E213.top");var subQ20=sQuery(id+"F18.wireOp",EDGE,"E213.left");var subQ21=sQuery(id+"F18.wireOp",EDGE,"E228.MirrorCS");var subQ22=sQuery(id+"F18.wireOp",EDGE,"E229.MirrorCS");var subQ23=sQuery(id+"F18.wireOp",EDGE,"E230.top");var subQ24=sQuery(id+"F18.wireOp",EDGE,"E230.left");var subQ25=sQuery(id+"F18.wireOp",EDGE,"E230.right");var subQ26=sQuery(id+"F18.wireOp",EDGE,"E231");Q0=makeQuery(id+"F28.boolean.opBoolean","MERGE",FACE,{"derivedFrom":[makeQuery(id+"F25.boolean.opBoolean","SPLIT",FACE,{"disambiguationData":[TD([makeQuery(id+"F17.opExtrude","SWEPT_FACE",FACE,{"disambiguationData":[OSD([sQuery(id+"F16.wireOp",EDGE,"E186")])]})])],"derivedFrom":makeQuery(id+"F19.opExtrude","CAP_FACE",FACE,{"disambiguationData":[OSD([subQ2,sQuery(id+"F18.wireOp",EDGE,"E191.top"),subQ1,subQ0,subQ18,subQ19,subQ20,subQ16,subQ17,subQ15,subQ13,subQ12,subQ11,subQ10,subQ9,subQ8,subQ7,subQ6,subQ5,subQ4,subQ3,subQ14,subQ21,subQ22,subQ23,subQ24,subQ25,subQ26])],"isStart":false})}),makeQuery(id+"F28.opExtrude","CAP_FACE",FACE,{"disambiguationData":[OSD([subQ2,subQ1,subQ0,sQuery(id+"F27.wireOp",EDGE,"E250"),sQuery(id+"F27.wireOp",EDGE,"E251"),sQuery(id+"F27.wireOp",EDGE,"E252"),sQuery(id+"F27.wireOp",EDGE,"E253"),sQuery(id+"F27.wireOp",EDGE,"E254"),sQuery(id+"F27.wireOp",EDGE,"E255.filletArc"),sQuery(id+"F27.wireOp",EDGE,"E256.filletArc"),sQuery(id+"F27.wireOp",EDGE,"E257.filletArc"),sQuery(id+"F27.wireOp",EDGE,"E258.filletArc")])],"isStart":false})]});}
            var sketch = newSketch(context, id + "F34", { "sketchPlane" : qUnion([Q0])});
            skLineSegment(sketch, "E266", {"start": v(-437.72, 315.78) * mm, "end": v(-404.29, 315.78) * mm});
            skArc(sketch, "E267", {"start": v(-437.72, 343.05) * mm, "mid": v(-446.74, 329.42) * mm, "end": v(-437.72, 315.78) * mm});
            skLineSegment(sketch, "E268", {"start": v(-437.72, 343.05) * mm, "end": v(-406, 343.05) * mm});
            skArc(sketch, "E269", {"start": v(-404.29, 315.78) * mm, "mid": v(-397.32, 329.91) * mm, "end": v(-406, 343.05) * mm});
            skLineSegment(sketch, "E270", {"start": v(-438.17, 301.67) * mm, "end": v(-406.71, 301.67) * mm});
            skLineSegment(sketch, "E271", {"start": v(-436.62, 273.98) * mm, "end": v(-407.46, 273.98) * mm});
            skArc(sketch, "E272", {"start": v(-407.46, 273.98) * mm, "mid": v(-396.88, 287.55) * mm, "end": v(-406.71, 301.67) * mm});
            skArc(sketch, "E273", {"start": v(-438.56, 301.8) * mm, "mid": v(-446.55, 287.27) * mm, "end": v(-436.62, 273.98) * mm});
            skSolve(sketch);
        }
        {
            var Q0;
            Q0=makeQuery(id+"F17.opExtrude","CAP_FACE",FACE,{"disambiguationData":[OSD([sQuery(id+"F16.wireOp",EDGE,"E182.bottom"),sQuery(id+"F16.wireOp",EDGE,"E182.top"),sQuery(id+"F16.wireOp",EDGE,"E182.left"),sQuery(id+"F16.wireOp",EDGE,"E182.right")])],"isStart":false});
            var Q1;
            Q1=makeQuery(id+"F34.imprint","IMPRINT",FACE,{"disambiguationData":[TD([[makeQuery(id+"F34.imprint","IMPRINT",EDGE,{"derivedFrom":sQuery(id+"F34.wireOp",EDGE,"E266")}),1.0]])]});
            extrude(context, id + "F35", {"entities" : qUnion([Q0, Q1]), "operationType" : NewBodyOperationType.ADD, "depth" : 2.54 * mm, "offsetDistance" : 25.4 * mm});
        }
        {
            var Q0;
            {var subQ0=sQuery(id+"F18.wireOp",EDGE,"E191.right");var subQ1=sQuery(id+"F18.wireOp",EDGE,"E191.left");var subQ2=sQuery(id+"F18.wireOp",EDGE,"E191.bottom");var subQ3=sQuery(id+"F18.wireOp",EDGE,"E226.MirrorCS");var subQ4=sQuery(id+"F18.wireOp",EDGE,"E225.MirrorCS");var subQ5=sQuery(id+"F18.wireOp",EDGE,"E224.MirrorCS");var subQ6=sQuery(id+"F18.wireOp",EDGE,"E223.MirrorCS");var subQ7=sQuery(id+"F18.wireOp",EDGE,"E222.MirrorCS");var subQ8=sQuery(id+"F18.wireOp",EDGE,"E219");var subQ9=sQuery(id+"F18.wireOp",EDGE,"E218.MirrorCS");var subQ10=sQuery(id+"F18.wireOp",EDGE,"E217.MirrorCS");var subQ11=sQuery(id+"F18.wireOp",EDGE,"E216.MirrorCS");var subQ12=sQuery(id+"F18.wireOp",EDGE,"E215");var subQ13=sQuery(id+"F18.wireOp",EDGE,"E214.right");var subQ14=sQuery(id+"F18.wireOp",EDGE,"E227.MirrorCS");var subQ15=sQuery(id+"F18.wireOp",EDGE,"E214.left");var subQ16=sQuery(id+"F18.wireOp",EDGE,"E213.right");var subQ17=sQuery(id+"F18.wireOp",EDGE,"E214.top");var subQ18=sQuery(id+"F18.wireOp",EDGE,"E213.bottom");var subQ19=sQuery(id+"F18.wireOp",EDGE,"E213.top");var subQ20=sQuery(id+"F18.wireOp",EDGE,"E213.left");var subQ21=sQuery(id+"F18.wireOp",EDGE,"E228.MirrorCS");var subQ22=sQuery(id+"F18.wireOp",EDGE,"E229.MirrorCS");var subQ23=sQuery(id+"F18.wireOp",EDGE,"E230.top");var subQ24=sQuery(id+"F18.wireOp",EDGE,"E230.left");var subQ25=sQuery(id+"F18.wireOp",EDGE,"E230.right");var subQ26=sQuery(id+"F18.wireOp",EDGE,"E231");Q0=makeQuery(id+"F28.boolean.opBoolean","MERGE",FACE,{"derivedFrom":[makeQuery(id+"F25.boolean.opBoolean","SPLIT",FACE,{"disambiguationData":[TD([makeQuery(id+"F17.opExtrude","SWEPT_FACE",FACE,{"disambiguationData":[OSD([sQuery(id+"F16.wireOp",EDGE,"E186")])]})])],"derivedFrom":makeQuery(id+"F19.opExtrude","CAP_FACE",FACE,{"disambiguationData":[OSD([subQ2,sQuery(id+"F18.wireOp",EDGE,"E191.top"),subQ1,subQ0,subQ18,subQ19,subQ20,subQ16,subQ17,subQ15,subQ13,subQ12,subQ11,subQ10,subQ9,subQ8,subQ7,subQ6,subQ5,subQ4,subQ3,subQ14,subQ21,subQ22,subQ23,subQ24,subQ25,subQ26])],"isStart":false})}),makeQuery(id+"F28.opExtrude","CAP_FACE",FACE,{"disambiguationData":[OSD([subQ2,subQ1,subQ0,sQuery(id+"F27.wireOp",EDGE,"E250"),sQuery(id+"F27.wireOp",EDGE,"E251"),sQuery(id+"F27.wireOp",EDGE,"E252"),sQuery(id+"F27.wireOp",EDGE,"E253"),sQuery(id+"F27.wireOp",EDGE,"E254"),sQuery(id+"F27.wireOp",EDGE,"E255.filletArc"),sQuery(id+"F27.wireOp",EDGE,"E256.filletArc"),sQuery(id+"F27.wireOp",EDGE,"E257.filletArc"),sQuery(id+"F27.wireOp",EDGE,"E258.filletArc")])],"isStart":false})]});}
            var sketch = newSketch(context, id + "F36", { "sketchPlane" : qUnion([Q0])});
            skLineSegment(sketch, "E274", {"start": v(-439.02, 303.04) * mm, "end": v(-405.47, 303.04) * mm});
            skLineSegment(sketch, "E275", {"start": v(-438.22, 272.94) * mm, "end": v(-404.9, 272.94) * mm});
            skArc(sketch, "E276", {"start": v(-404.9, 272.94) * mm, "mid": v(-394.05, 288.2) * mm, "end": v(-405.47, 303.04) * mm});
            skArc(sketch, "E277", {"start": v(-439.02, 303.04) * mm, "mid": v(-447.88, 287.75) * mm, "end": v(-438.22, 272.94) * mm});
            skSolve(sketch);
        }
        {
            var Q0;
            Q0=makeQuery(id+"F36.imprint","IMPRINT",FACE,{"disambiguationData":[TD([[makeQuery(id+"F36.imprint","IMPRINT",EDGE,{"derivedFrom":sQuery(id+"F36.wireOp",EDGE,"E274")}),-1.0]])]});
            extrude(context, id + "F37", {"entities" : qUnion([Q0]), "operationType" : NewBodyOperationType.ADD, "depth" : 2.54 * mm, "offsetDistance" : 25.4 * mm});
        }
        {
            var Q0;
            Q0=makeQuery(id+"F1.opExtrude","CAP_FACE",FACE,{"disambiguationData":[OSD([sQuery(id+"F0.wireOp",EDGE,"E0.bottom"),sQuery(id+"F0.wireOp",EDGE,"E0.top"),sQuery(id+"F0.wireOp",EDGE,"E0.left"),sQuery(id+"F0.wireOp",EDGE,"E0.right"),sQuery(id+"F0.wireOp",EDGE,"E9"),sQuery(id+"F0.wireOp",EDGE,"E10"),sQuery(id+"F0.wireOp",EDGE,"E11"),sQuery(id+"F0.wireOp",EDGE,"E12"),sQuery(id+"F0.wireOp",EDGE,"E13.filletArc"),sQuery(id+"F0.wireOp",EDGE,"E14.bottom"),sQuery(id+"F0.wireOp",EDGE,"E14.top"),sQuery(id+"F0.wireOp",EDGE,"E14.left"),sQuery(id+"F0.wireOp",EDGE,"E14.right"),sQuery(id+"F0.wireOp",EDGE,"E15.filletArc"),sQuery(id+"F0.wireOp",EDGE,"E17.filletArc"),sQuery(id+"F0.wireOp",EDGE,"E18.filletArc"),sQuery(id+"F0.wireOp",EDGE,"E19"),sQuery(id+"F0.wireOp",EDGE,"E20"),sQuery(id+"F0.wireOp",EDGE,"E21.top"),sQuery(id+"F0.wireOp",EDGE,"E21.left"),sQuery(id+"F0.wireOp",EDGE,"E22.bottom"),sQuery(id+"F0.wireOp",EDGE,"E22.top"),sQuery(id+"F0.wireOp",EDGE,"E22.left"),sQuery(id+"F0.wireOp",EDGE,"E22.right"),sQuery(id+"F0.wireOp",EDGE,"E23.filletArc"),sQuery(id+"F0.wireOp",EDGE,"E24.filletArc"),sQuery(id+"F0.wireOp",EDGE,"E26.MirrorCS"),sQuery(id+"F0.wireOp",EDGE,"E27.MirrorCS"),sQuery(id+"F0.wireOp",EDGE,"E28"),sQuery(id+"F0.wireOp",EDGE,"E30"),sQuery(id+"F0.wireOp",EDGE,"E33.MirrorCS"),sQuery(id+"F0.wireOp",EDGE,"E34.MirrorCS"),sQuery(id+"F0.wireOp",EDGE,"E35.MirrorCS"),sQuery(id+"F0.wireOp",EDGE,"E36.MirrorCS"),sQuery(id+"F0.wireOp",EDGE,"E37"),sQuery(id+"F0.wireOp",EDGE,"E38"),sQuery(id+"F0.wireOp",EDGE,"E39"),sQuery(id+"F0.wireOp",EDGE,"E40"),sQuery(id+"F0.wireOp",EDGE,"E43.bottom"),sQuery(id+"F0.wireOp",EDGE,"E43.top"),sQuery(id+"F0.wireOp",EDGE,"E43.left"),sQuery(id+"F0.wireOp",EDGE,"E43.right"),sQuery(id+"F0.wireOp",EDGE,"E45.MirrorCS"),sQuery(id+"F0.wireOp",EDGE,"E46.MirrorCS"),sQuery(id+"F0.wireOp",EDGE,"E47"),sQuery(id+"F0.wireOp",EDGE,"E48"),sQuery(id+"F0.wireOp",EDGE,"E50.MirrorCS"),sQuery(id+"F0.wireOp",EDGE,"E51.MirrorCS"),sQuery(id+"F0.wireOp",EDGE,"E52.MirrorCS"),sQuery(id+"F0.wireOp",EDGE,"E53.MirrorCS"),sQuery(id+"F0.wireOp",EDGE,"E54"),sQuery(id+"F0.wireOp",EDGE,"E55"),sQuery(id+"F0.wireOp",EDGE,"E56"),sQuery(id+"F0.wireOp",EDGE,"E57"),sQuery(id+"F0.wireOp",EDGE,"E58")])],"isStart":false});
            var sketch = newSketch(context, id + "F38", { "sketchPlane" : qUnion([Q0])});
            skLineSegment(sketch, "E278.top", {"start": v(-508, 1663.7) * mm, "end": v(-495.3, 1663.7) * mm});
            skLineSegment(sketch, "E278.left", {"start": v(-508, 1676.4) * mm, "end": v(-508, 1663.7) * mm});
            skLineSegment(sketch, "E278.right", {"start": v(-495.3, 1676.4) * mm, "end": v(-495.3, 1663.7) * mm, "construction": true});
            skLineSegment(sketch, "E279", {"start": v(-508, 1663.7) * mm, "end": v(-495.3, 1676.4) * mm, "construction": true});
            skLineSegment(sketch, "E280", {"start": v(-508, 1676.4) * mm, "end": v(-495.3, 1663.7) * mm, "construction": true});
            skCircle(sketch, "E281", {"center": v(-501.65, 1670.05) * mm, "radius": 6.2 * mm});
            skSolve(sketch);
        }
        {
            var Q0;
            Q0 = qSketchRegion(id + "F38", true);
            extrude(context, id + "F39", {"entities" : qUnion([Q0]), "operationType" : NewBodyOperationType.REMOVE, "oppositeDirection" : true, "depth" : 1.27 * mm, "offsetDistance" : 25.4 * mm});
        }
        {
            var Q0;
            Q0=makeQuery(id+"F17.opExtrude","CAP_FACE",FACE,{"disambiguationData":[OSD([sQuery(id+"F16.wireOp",EDGE,"E190.bottom"),sQuery(id+"F16.wireOp",EDGE,"E190.top"),sQuery(id+"F16.wireOp",EDGE,"E190.left"),sQuery(id+"F16.wireOp",EDGE,"E190.right")])],"isStart":false});
            var sketch = newSketch(context, id + "F40", { "sketchPlane" : qUnion([Q0])});
            skLineSegment(sketch, "E282.bottom", {"start": v(-495.25, 1670.67) * mm, "end": v(-482.55, 1670.67) * mm});
            skLineSegment(sketch, "E282.top", {"start": v(-495.25, 1657.97) * mm, "end": v(-482.55, 1657.97) * mm});
            skLineSegment(sketch, "E282.left", {"start": v(-495.25, 1670.67) * mm, "end": v(-495.25, 1657.97) * mm});
            skLineSegment(sketch, "E282.right", {"start": v(-482.55, 1670.67) * mm, "end": v(-482.55, 1657.97) * mm});
            skSolve(sketch);
        }
        {
            var Q0;
            Q0 = qSketchRegion(id + "F40", true);
            extrude(context, id + "F41", {"entities" : qUnion([Q0]), "operationType" : NewBodyOperationType.ADD, "depth" : 12.7 * mm, "offsetDistance" : 25.4 * mm});
        }
        {
            var Q0;
            {var subQ0=sQuery(id+"F13.wireOp",EDGE,"E180.left");var subQ1=sQuery(id+"F13.wireOp",EDGE,"E180.top");Q0=makeQuery(id+"F33.opBoolean","SPLIT",FACE,{"disambiguationData":[TD([makeQuery(id+"F15.opShell","OFFSET_FACE",FACE,{"disambiguationData":[OSD([subQ1])]})])],"derivedFrom":makeQuery(id+"F15.opShell","OFFSET_FACE",FACE,{"disambiguationData":[OSD([subQ0])]})});}
            var sketch = newSketch(context, id + "F42", { "sketchPlane" : qUnion([Q0])});
            skLineSegment(sketch, "E283.bottom", {"start": v(-245, 2.54) * mm, "end": v(-230.74, 2.54) * mm});
            skLineSegment(sketch, "E283.top", {"start": v(-245, 256.54) * mm, "end": v(-230.74, 256.54) * mm});
            skLineSegment(sketch, "E283.left", {"start": v(-245, 2.54) * mm, "end": v(-245, 256.54) * mm});
            skLineSegment(sketch, "E283.right", {"start": v(-230.74, 2.54) * mm, "end": v(-230.74, 256.54) * mm});
            skSolve(sketch);
        }
        {
            var Q0;
            Q0 = qSketchRegion(id + "F42", true);
            extrude(context, id + "F43", {"entities" : qUnion([Q0]), "operationType" : NewBodyOperationType.ADD, "depth" : 406.4 * mm, "offsetDistance" : 25.4 * mm, "hasSecondDirection" : true, "secondDirectionOppositeDirection" : false, "secondDirectionDepth" : 50.8 * mm});
        }
        {
            var Q0;
            Q0=makeQuery(id+"F10.opExtrude","CAP_EDGE",EDGE,{"disambiguationData":[OSD([sQuery(id+"F9.wireOp",EDGE,"E163")])],"isStart":true});
            var Q1;
            Q1=makeQuery(id+"F10.opExtrude","CAP_EDGE",EDGE,{"disambiguationData":[OSD([sQuery(id+"F9.wireOp",EDGE,"E164")])],"isStart":true});
            var Q2;
            Q2=makeQuery(id+"F10.opExtrude","CAP_EDGE",EDGE,{"disambiguationData":[OSD([sQuery(id+"F9.wireOp",EDGE,"E165"),sQuery(id+"F9.wireOp",EDGE,"E166.MirrorCS")])],"isStart":true});
            var Q3;
            Q3=makeQuery(id+"F10.opExtrude","CAP_EDGE",EDGE,{"disambiguationData":[OSD([sQuery(id+"F9.wireOp",EDGE,"E169.MirrorCS")])],"isStart":true});
            var Q4;
            Q4=makeQuery(id+"F10.opExtrude","CAP_EDGE",EDGE,{"disambiguationData":[OSD([sQuery(id+"F9.wireOp",EDGE,"E162"),sQuery(id+"F9.wireOp",EDGE,"E167.MirrorCS")])],"isStart":false});
            var Q5;
            Q5=makeQuery(id+"F10.opExtrude","CAP_EDGE",EDGE,{"disambiguationData":[OSD([sQuery(id+"F9.wireOp",EDGE,"E163")])],"isStart":false});
            var Q6;
            Q6=makeQuery(id+"F10.opExtrude","SWEPT_FACE",FACE,{"disambiguationData":[OSD([sQuery(id+"F9.wireOp",EDGE,"E163")])]});
            var Q7;
            Q7=makeQuery(id+"F10.opExtrude","SWEPT_EDGE",EDGE,{"disambiguationData":[OSD([sQuery(id+"F9.wireOp",EDGE,"E167.MirrorCS"),sQuery(id+"F9.wireOp",EDGE,"E168.MirrorCS")])]});
            var Q8;
            Q8=makeQuery(id+"F10.opExtrude","CAP_EDGE",EDGE,{"disambiguationData":[OSD([sQuery(id+"F9.wireOp",EDGE,"E168.MirrorCS")])],"isStart":true});
            var Q9;
            Q9=makeQuery(id+"F10.opExtrude","CAP_EDGE",EDGE,{"disambiguationData":[OSD([sQuery(id+"F9.wireOp",EDGE,"E168.MirrorCS")])],"isStart":false});
            var Q10;
            Q10=makeQuery(id+"F10.opExtrude","CAP_EDGE",EDGE,{"disambiguationData":[OSD([sQuery(id+"F9.wireOp",EDGE,"E162"),sQuery(id+"F9.wireOp",EDGE,"E167.MirrorCS")])],"isStart":true});
            var Q11;
            Q11=makeQuery(id+"F10.opExtrude","CAP_EDGE",EDGE,{"disambiguationData":[OSD([sQuery(id+"F9.wireOp",EDGE,"E165"),sQuery(id+"F9.wireOp",EDGE,"E166.MirrorCS")])],"isStart":false});
            var Q12;
            Q12=makeQuery(id+"F10.opExtrude","CAP_EDGE",EDGE,{"disambiguationData":[OSD([sQuery(id+"F9.wireOp",EDGE,"E164")])],"isStart":false});
            var Q13;
            Q13=makeQuery(id+"F10.opExtrude","CAP_EDGE",EDGE,{"disambiguationData":[OSD([sQuery(id+"F9.wireOp",EDGE,"E169.MirrorCS")])],"isStart":false});
            fillet(context, id + "F44", {"entities" : qUnion([Q0, Q1, Q2, Q3, Q4, Q5, Q6, Q7, Q8, Q9, Q10, Q11, Q12, Q13]), "radius" : 5.08 * mm, "tangentPropagation" : true, "allowEdgeOverflow" : false});
        }
        {
            var Q0;
            Q0=makeQuery(id+"F35.opExtrude","CAP_EDGE",EDGE,{"disambiguationData":[OSD([sQuery(id+"F16.wireOp",EDGE,"E182.bottom")])],"isStart":false});
            var Q1;
            Q1=makeQuery(id+"F35.opExtrude","CAP_EDGE",EDGE,{"disambiguationData":[OSD([sQuery(id+"F16.wireOp",EDGE,"E182.top")])],"isStart":false});
            fillet(context, id + "F45", {"entities" : qUnion([Q0, Q1]), "radius" : 3.8 * mm, "tangentPropagation" : true, "allowEdgeOverflow" : false});
        }
    });
